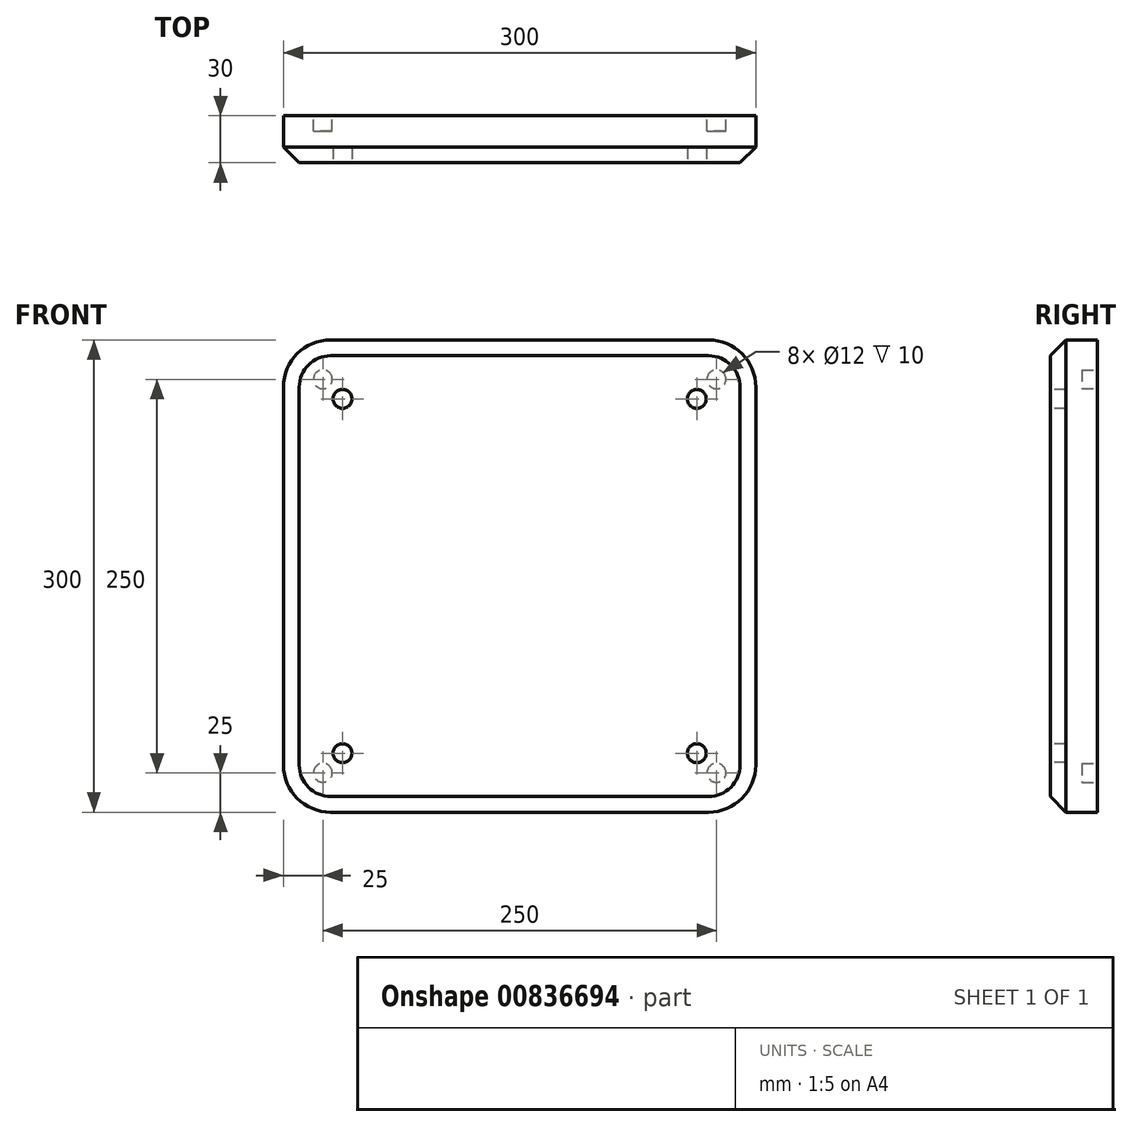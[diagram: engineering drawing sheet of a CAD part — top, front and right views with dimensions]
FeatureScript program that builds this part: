
annotation { "Feature Type Name" : "Feature", "Feature Type Description" : "" }
export const myFeature = defineFeature(function(context is Context, id is Id, definition is map)
    precondition{}
    {
        {
            var Q0;
            Q0=qCreatedBy(makeId("Front.planeOp"),FACE);
            var sketch = newSketch(context, id + "F0", { "sketchPlane" : qUnion([Q0])});
            skLineSegment(sketch, "E0.bottom", {"start": v(-120, 150) * mm, "end": v(120, 150) * mm});
            skLineSegment(sketch, "E0.top", {"start": v(-120, -150) * mm, "end": v(120, -150) * mm});
            skLineSegment(sketch, "E0.left", {"start": v(-150, 120) * mm, "end": v(-150, -120) * mm});
            skLineSegment(sketch, "E0.right", {"start": v(150, 120) * mm, "end": v(150, -120) * mm});
            skPoint(sketch, "E0.middle", {"position": v(0, 0) * mm});
            skPoint(sketch, "E1.visualSharp", {"position": v(-150, 150) * mm});
            skArc(sketch, "E1.filletArc", {"start": v(-120, 150) * mm, "mid": v(-141.21, 141.21) * mm, "end": v(-150, 120) * mm});
            skPoint(sketch, "E2.visualSharp", {"position": v(150, 150) * mm});
            skArc(sketch, "E2.filletArc", {"start": v(150, 120) * mm, "mid": v(141.21, 141.21) * mm, "end": v(120, 150) * mm});
            skPoint(sketch, "E3.visualSharp", {"position": v(150, -150) * mm});
            skArc(sketch, "E3.filletArc", {"start": v(120, -150) * mm, "mid": v(141.21, -141.21) * mm, "end": v(150, -120) * mm});
            skPoint(sketch, "E4.visualSharp", {"position": v(-150, -150) * mm});
            skArc(sketch, "E4.filletArc", {"start": v(-150, -120) * mm, "mid": v(-141.21, -141.21) * mm, "end": v(-120, -150) * mm});
            skSolve(sketch);
        }
        {
            var Q0;
            Q0 = qSketchRegion(id + "F0", true);
            extrude(context, id + "F1", {"entities" : qUnion([Q0]), "depth" : 30 * mm, "offsetDistance" : 25 * mm});
        }
        {
            var Q0;
            Q0=makeQuery(id+"F1.opExtrude","CAP_EDGE",EDGE,{"disambiguationData":[OSD([sQuery(id+"F0.wireOp",EDGE,"E0.bottom")])],"isStart":false});
            var Q1;
            Q1=makeQuery(id+"F1.opExtrude","CAP_EDGE",EDGE,{"disambiguationData":[OSD([sQuery(id+"F0.wireOp",EDGE,"E0.left")])],"isStart":false});
            var Q2;
            Q2=makeQuery(id+"F1.opExtrude","CAP_EDGE",EDGE,{"disambiguationData":[OSD([sQuery(id+"F0.wireOp",EDGE,"E0.top")])],"isStart":false});
            var Q3;
            Q3=makeQuery(id+"F1.opExtrude","CAP_EDGE",EDGE,{"disambiguationData":[OSD([sQuery(id+"F0.wireOp",EDGE,"E0.right")])],"isStart":false});
            var Q4;
            Q4=makeQuery(id+"F1.opExtrude","CAP_EDGE",EDGE,{"disambiguationData":[OSD([sQuery(id+"F0.wireOp",EDGE,"E2.filletArc")])],"isStart":false});
            var Q5;
            Q5=makeQuery(id+"F1.opExtrude","CAP_EDGE",EDGE,{"disambiguationData":[OSD([sQuery(id+"F0.wireOp",EDGE,"E1.filletArc")])],"isStart":false});
            var Q6;
            Q6=makeQuery(id+"F1.opExtrude","CAP_EDGE",EDGE,{"disambiguationData":[OSD([sQuery(id+"F0.wireOp",EDGE,"E4.filletArc")])],"isStart":false});
            var Q7;
            Q7=makeQuery(id+"F1.opExtrude","CAP_EDGE",EDGE,{"disambiguationData":[OSD([sQuery(id+"F0.wireOp",EDGE,"E3.filletArc")])],"isStart":false});
            chamfer(context, id + "F2", {"entities" : qUnion([Q0, Q1, Q2, Q3, Q4, Q5, Q6, Q7]), "width" : 10 * mm, "tangentPropagation" : true});
        }
        {
            var Q0;
            Q0=makeQuery(id+"F1.opExtrude","CAP_FACE",FACE,{"disambiguationData":[OSD([sQuery(id+"F0.wireOp",EDGE,"E0.bottom"),sQuery(id+"F0.wireOp",EDGE,"E0.top"),sQuery(id+"F0.wireOp",EDGE,"E0.left"),sQuery(id+"F0.wireOp",EDGE,"E0.right"),sQuery(id+"F0.wireOp",EDGE,"E1.filletArc"),sQuery(id+"F0.wireOp",EDGE,"E2.filletArc"),sQuery(id+"F0.wireOp",EDGE,"E3.filletArc"),sQuery(id+"F0.wireOp",EDGE,"E4.filletArc")])],"isStart":false});
            var sketch = newSketch(context, id + "F3", { "sketchPlane" : qUnion([Q0])});
            skLineSegment(sketch, "E5.bottom", {"start": v(-112.5, 112.5) * mm, "end": v(112.5, 112.5) * mm, "construction": true});
            skLineSegment(sketch, "E5.top", {"start": v(-112.5, -112.5) * mm, "end": v(112.5, -112.5) * mm, "construction": true});
            skLineSegment(sketch, "E5.left", {"start": v(-112.5, 112.5) * mm, "end": v(-112.5, -112.5) * mm, "construction": true});
            skLineSegment(sketch, "E5.right", {"start": v(112.5, 112.5) * mm, "end": v(112.5, -112.5) * mm, "construction": true});
            skPoint(sketch, "E5.middle", {"position": v(0, 0) * mm});
            skCircle(sketch, "E6", {"center": v(-112.5, 112.5) * mm, "radius": 6 * mm});
            skCircle(sketch, "E7", {"center": v(-112.5, -112.5) * mm, "radius": 6 * mm});
            skCircle(sketch, "E8", {"center": v(112.5, -112.5) * mm, "radius": 6 * mm});
            skCircle(sketch, "E9", {"center": v(112.5, 112.5) * mm, "radius": 6 * mm});
            skSolve(sketch);
        }
        {
            var Q0;
            Q0 = qSketchRegion(id + "F3", true);
            extrude(context, id + "F4", {"entities" : qUnion([Q0]), "operationType" : NewBodyOperationType.REMOVE, "oppositeDirection" : true, "depth" : 10 * mm, "offsetDistance" : 25 * mm});
        }
        {
            var Q0;
            Q0=makeQuery(id+"F1.opExtrude","CAP_FACE",FACE,{"disambiguationData":[OSD([sQuery(id+"F0.wireOp",EDGE,"E0.bottom"),sQuery(id+"F0.wireOp",EDGE,"E0.top"),sQuery(id+"F0.wireOp",EDGE,"E0.left"),sQuery(id+"F0.wireOp",EDGE,"E0.right"),sQuery(id+"F0.wireOp",EDGE,"E1.filletArc"),sQuery(id+"F0.wireOp",EDGE,"E2.filletArc"),sQuery(id+"F0.wireOp",EDGE,"E3.filletArc"),sQuery(id+"F0.wireOp",EDGE,"E4.filletArc")])],"isStart":true});
            var sketch = newSketch(context, id + "F5", { "sketchPlane" : qUnion([Q0])});
            skLineSegment(sketch, "E10.bottom", {"start": v(-125, 125) * mm, "end": v(125, 125) * mm, "construction": true});
            skLineSegment(sketch, "E10.top", {"start": v(-125, -125) * mm, "end": v(125, -125) * mm, "construction": true});
            skLineSegment(sketch, "E10.left", {"start": v(-125, 125) * mm, "end": v(-125, -125) * mm, "construction": true});
            skLineSegment(sketch, "E10.right", {"start": v(125, 125) * mm, "end": v(125, -125) * mm, "construction": true});
            skPoint(sketch, "E10.middle", {"position": v(0, 0) * mm});
            skCircle(sketch, "E11", {"center": v(-125, 125) * mm, "radius": 6 * mm});
            skCircle(sketch, "E12", {"center": v(-125, -125) * mm, "radius": 6 * mm});
            skCircle(sketch, "E13", {"center": v(125, -125) * mm, "radius": 6 * mm});
            skCircle(sketch, "E14", {"center": v(125, 125) * mm, "radius": 6 * mm});
            skSolve(sketch);
        }
        {
            var Q0;
            Q0 = qSketchRegion(id + "F5", true);
            extrude(context, id + "F6", {"entities" : qUnion([Q0]), "operationType" : NewBodyOperationType.REMOVE, "oppositeDirection" : true, "depth" : 10 * mm, "offsetDistance" : 25 * mm});
        }
    });
